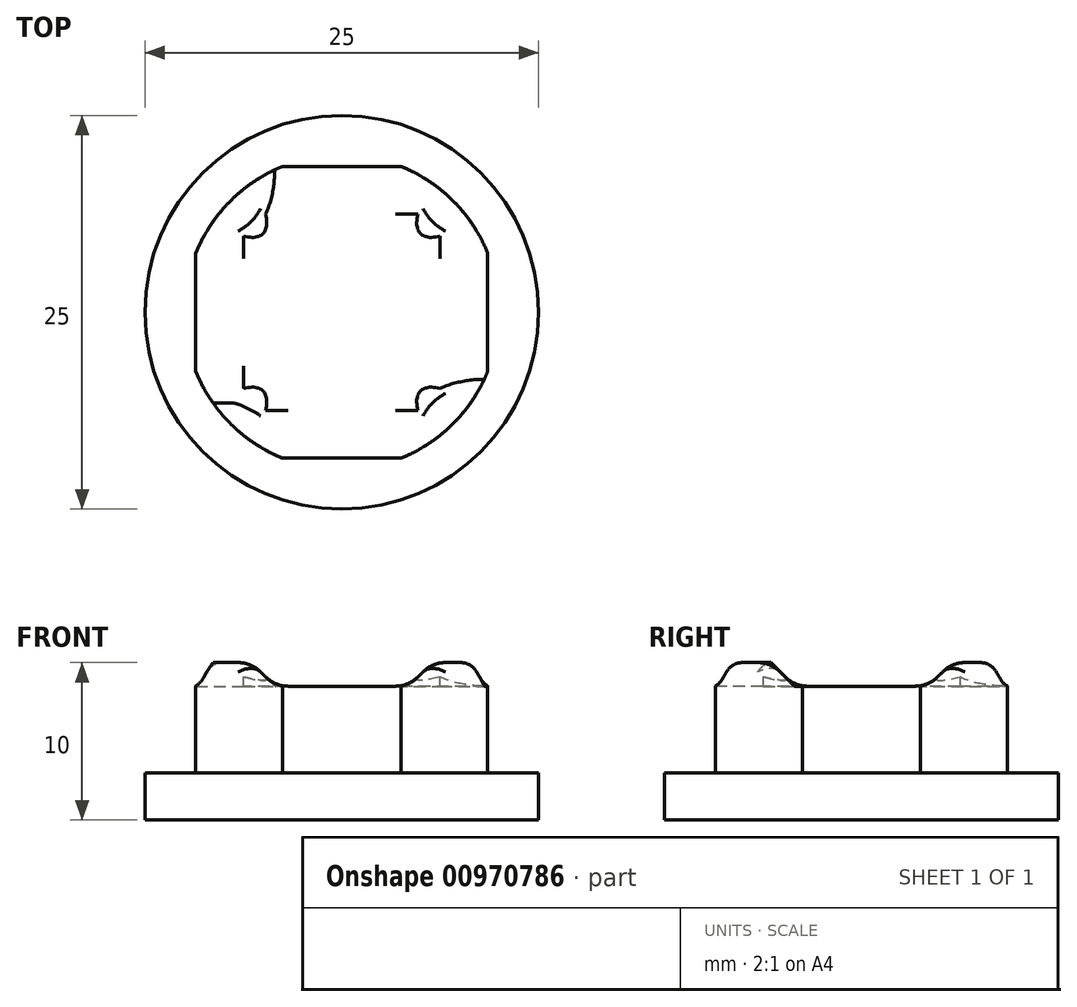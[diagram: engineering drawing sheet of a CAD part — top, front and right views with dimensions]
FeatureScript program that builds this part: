
annotation { "Feature Type Name" : "Feature", "Feature Type Description" : "" }
export const myFeature = defineFeature(function(context is Context, id is Id, definition is map)
    precondition{}
    {
        {
            var Q0;
            Q0=qCreatedBy(makeId("Top.planeOp"),FACE);
            var sketch = newSketch(context, id + "F0", { "sketchPlane" : qUnion([Q0])});
            skCircle(sketch, "E0", {"center": v(0, 0) * mm, "radius": 12.5 * mm});
            skSolve(sketch);
        }
        {
            var Q0;
            Q0 = qSketchRegion(id + "F0", true);
            extrude(context, id + "F1", {"entities" : qUnion([Q0]), "depth" : 3 * mm, "offsetDistance" : 25 * mm});
        }
        {
            var Q0;
            Q0=qCreatedBy(makeId("Top.planeOp"),FACE);
            var sketch = newSketch(context, id + "F2", { "sketchPlane" : qUnion([Q0])});
            skLineSegment(sketch, "E1.bottom", {"start": v(9.27, -3.75) * mm, "end": v(3.75, -3.75) * mm});
            skLineSegment(sketch, "E1.top", {"start": v(9.27, 3.75) * mm, "end": v(3.75, 3.75) * mm});
            skLineSegment(sketch, "E1.left", {"start": v(9.27, -3.75) * mm, "end": v(9.27, 3.75) * mm});
            skLineSegment(sketch, "E1.right", {"start": v(-9.27, -3.75) * mm, "end": v(-9.27, 3.75) * mm});
            skPoint(sketch, "E1.middle", {"position": v(0, 0) * mm});
            skLineSegment(sketch, "E2.bottom", {"start": v(3.75, 9.27) * mm, "end": v(-3.75, 9.27) * mm});
            skLineSegment(sketch, "E2.top", {"start": v(3.75, -9.27) * mm, "end": v(-3.75, -9.27) * mm});
            skLineSegment(sketch, "E2.left", {"start": v(3.75, 9.27) * mm, "end": v(3.75, 3.75) * mm});
            skLineSegment(sketch, "E2.right", {"start": v(-3.75, 9.27) * mm, "end": v(-3.75, 3.75) * mm});
            skLineSegment(sketch, "E3.trimOffspring", {"start": v(-3.75, -3.75) * mm, "end": v(-9.27, -3.75) * mm});
            skLineSegment(sketch, "E4.trimOffspring", {"start": v(-3.75, -3.75) * mm, "end": v(-3.75, -9.27) * mm});
            skLineSegment(sketch, "E5.trimOffspring", {"start": v(-3.75, 3.75) * mm, "end": v(-9.27, 3.75) * mm});
            skLineSegment(sketch, "E6.trimOffspring", {"start": v(3.75, -3.75) * mm, "end": v(3.75, -9.27) * mm});
            skSolve(sketch);
        }
        {
            var Q0;
            Q0 = qSketchRegion(id + "F2", true);
            extrude(context, id + "F3", {"entities" : qUnion([Q0]), "operationType" : NewBodyOperationType.ADD, "depth" : 8.5 * mm, "offsetDistance" : 25 * mm});
        }
        {
            var Q0;
            Q0=qCreatedBy(makeId("Top.planeOp"),FACE);
            var sketch = newSketch(context, id + "F4", { "sketchPlane" : qUnion([Q0])});
            skArc(sketch, "E7", {"start": v(-3.75, 9.27) * mm, "mid": v(-7.07, 7.07) * mm, "end": v(-9.27, 3.75) * mm});
            skLineSegment(sketch, "E8.left", {"start": v(3.75, -9.27) * mm, "end": v(3.75, -3.75) * mm});
            skLineSegment(sketch, "E8.right", {"start": v(-3.75, -9.27) * mm, "end": v(-3.75, -3.75) * mm});
            skLineSegment(sketch, "E9.bottom", {"start": v(9.27, -3.75) * mm, "end": v(3.75, -3.75) * mm});
            skLineSegment(sketch, "E9.top", {"start": v(9.27, 3.75) * mm, "end": v(3.75, 3.75) * mm});
            skLineSegment(sketch, "E10.trimOffspring", {"start": v(-3.75, 3.75) * mm, "end": v(-3.75, 9.27) * mm});
            skLineSegment(sketch, "E11.trimOffspring", {"start": v(-3.75, 3.75) * mm, "end": v(-9.27, 3.75) * mm});
            skLineSegment(sketch, "E12.trimOffspring", {"start": v(3.75, 3.75) * mm, "end": v(3.75, 9.27) * mm});
            skLineSegment(sketch, "E13.trimOffspring", {"start": v(-3.75, -3.75) * mm, "end": v(-9.27, -3.75) * mm});
            skArc(sketch, "E14.trimOffspring", {"start": v(-9.27, -3.75) * mm, "mid": v(-7.07, -7.07) * mm, "end": v(-3.75, -9.27) * mm});
            skArc(sketch, "E15.trimOffspring", {"start": v(3.75, -9.27) * mm, "mid": v(7.07, -7.07) * mm, "end": v(9.27, -3.75) * mm});
            skArc(sketch, "E16.trimOffspring", {"start": v(9.27, 3.75) * mm, "mid": v(7.07, 7.07) * mm, "end": v(3.75, 9.27) * mm});
            skSolve(sketch);
        }
        {
            var Q0;
            Q0 = qSketchRegion(id + "F4", true);
            extrude(context, id + "F5", {"entities" : qUnion([Q0]), "operationType" : NewBodyOperationType.ADD, "depth" : 10 * mm, "offsetDistance" : 25 * mm});
        }
        {
            var Q0;
            Q0=makeQuery(id+"F5.opExtrude","CAP_EDGE",EDGE,{"disambiguationData":[OSD([sQuery(id+"F4.wireOp",EDGE,"E12.trimOffspring")])],"isStart":false});
            chamfer(context, id + "F6", {"entities" : qUnion([Q0]), "width" : 2 * mm, "tangentPropagation" : true});
        }
        {
            var Q0;
            Q0=makeQuery(id+"F5.opExtrude","CAP_EDGE",EDGE,{"disambiguationData":[OSD([sQuery(id+"F4.wireOp",EDGE,"E9.top")])],"isStart":false});
            chamfer(context, id + "F7", {"entities" : qUnion([Q0]), "width" : 2 * mm, "tangentPropagation" : true});
        }
        {
            var Q0;
            Q0=makeQuery(id+"F5.opExtrude","CAP_EDGE",EDGE,{"disambiguationData":[OSD([sQuery(id+"F4.wireOp",EDGE,"E11.trimOffspring")])],"isStart":false});
            var Q1;
            Q1=makeQuery(id+"F5.opExtrude","CAP_EDGE",EDGE,{"disambiguationData":[OSD([sQuery(id+"F4.wireOp",EDGE,"E10.trimOffspring")])],"isStart":false});
            chamfer(context, id + "F8", {"entities" : qUnion([Q0, Q1]), "width" : 2 * mm, "tangentPropagation" : true});
        }
        {
            var Q0;
            Q0=makeQuery(id+"F5.opExtrude","CAP_EDGE",EDGE,{"disambiguationData":[OSD([sQuery(id+"F4.wireOp",EDGE,"E13.trimOffspring")])],"isStart":false});
            var Q1;
            Q1=makeQuery(id+"F5.opExtrude","CAP_EDGE",EDGE,{"disambiguationData":[OSD([sQuery(id+"F4.wireOp",EDGE,"E8.right")])],"isStart":false});
            var Q2;
            Q2=makeQuery(id+"F5.opExtrude","CAP_EDGE",EDGE,{"disambiguationData":[OSD([sQuery(id+"F4.wireOp",EDGE,"E8.left")])],"isStart":false});
            var Q3;
            Q3=makeQuery(id+"F5.opExtrude","CAP_EDGE",EDGE,{"disambiguationData":[OSD([sQuery(id+"F4.wireOp",EDGE,"E9.bottom")])],"isStart":false});
            chamfer(context, id + "F9", {"entities" : qUnion([Q0, Q1, Q2, Q3]), "width" : 2 * mm, "tangentPropagation" : true});
        }
        {
            var Q0;
            Q0=makeQuery(id+"F8.opChamfer","BLEND_EDGE",EDGE,{"blendedFrom":[makeQuery(id+"F5.opExtrude","CAP_EDGE",EDGE,{"disambiguationData":[OSD([sQuery(id+"F4.wireOp",EDGE,"E10.trimOffspring")])],"isStart":false}),makeQuery(id+"F5.opExtrude","CAP_EDGE",EDGE,{"disambiguationData":[OSD([sQuery(id+"F4.wireOp",EDGE,"E11.trimOffspring")])],"isStart":false})],"blendedInto":[]});
            var Q1;
            Q1=makeQuery(id+"F8.opChamfer","BLEND_EDGE",EDGE,{"blendedFrom":[makeQuery(id+"F5.opExtrude","CAP_EDGE",EDGE,{"disambiguationData":[OSD([sQuery(id+"F4.wireOp",EDGE,"E11.trimOffspring")])],"isStart":false}),makeQuery(id+"F3.opExtrude","CAP_FACE",FACE,{"disambiguationData":[OSD([sQuery(id+"F2.wireOp",EDGE,"E1.bottom"),sQuery(id+"F2.wireOp",EDGE,"E1.top"),sQuery(id+"F2.wireOp",EDGE,"E1.left"),sQuery(id+"F2.wireOp",EDGE,"E1.right"),sQuery(id+"F2.wireOp",EDGE,"E2.bottom"),sQuery(id+"F2.wireOp",EDGE,"E2.top"),sQuery(id+"F2.wireOp",EDGE,"E2.left"),sQuery(id+"F2.wireOp",EDGE,"E2.right"),sQuery(id+"F2.wireOp",EDGE,"E3.trimOffspring"),sQuery(id+"F2.wireOp",EDGE,"E4.trimOffspring"),sQuery(id+"F2.wireOp",EDGE,"E5.trimOffspring"),sQuery(id+"F2.wireOp",EDGE,"E6.trimOffspring")])],"isStart":false})],"blendedInto":[makeQuery(id+"F3.opExtrude","CAP_FACE",FACE,{"disambiguationData":[OSD([sQuery(id+"F2.wireOp",EDGE,"E1.bottom"),sQuery(id+"F2.wireOp",EDGE,"E1.top"),sQuery(id+"F2.wireOp",EDGE,"E1.left"),sQuery(id+"F2.wireOp",EDGE,"E1.right"),sQuery(id+"F2.wireOp",EDGE,"E2.bottom"),sQuery(id+"F2.wireOp",EDGE,"E2.top"),sQuery(id+"F2.wireOp",EDGE,"E2.left"),sQuery(id+"F2.wireOp",EDGE,"E2.right"),sQuery(id+"F2.wireOp",EDGE,"E3.trimOffspring"),sQuery(id+"F2.wireOp",EDGE,"E4.trimOffspring"),sQuery(id+"F2.wireOp",EDGE,"E5.trimOffspring"),sQuery(id+"F2.wireOp",EDGE,"E6.trimOffspring")])],"isStart":false})]});
            var Q2;
            {var subQ0=sQuery(id+"F4.wireOp",EDGE,"E11.trimOffspring");Q2=makeQuery(id+"F8.opChamfer","BLEND_EDGE",EDGE,{"blendedFrom":[makeQuery(id+"F5.opExtrude","CAP_EDGE",EDGE,{"disambiguationData":[OSD([subQ0])],"isStart":false}),makeQuery(id+"F5.opExtrude","CAP_FACE",FACE,{"disambiguationData":[OSD([sQuery(id+"F4.wireOp",EDGE,"E7"),sQuery(id+"F4.wireOp",EDGE,"E10.trimOffspring"),subQ0])],"isStart":false})],"blendedInto":[makeQuery(id+"F5.opExtrude","CAP_FACE",FACE,{"disambiguationData":[OSD([sQuery(id+"F4.wireOp",EDGE,"E7"),sQuery(id+"F4.wireOp",EDGE,"E10.trimOffspring"),subQ0])],"isStart":false})]});}
            var Q3;
            {var subQ0=sQuery(id+"F4.wireOp",EDGE,"E10.trimOffspring");Q3=makeQuery(id+"F8.opChamfer","BLEND_EDGE",EDGE,{"blendedFrom":[makeQuery(id+"F5.opExtrude","CAP_EDGE",EDGE,{"disambiguationData":[OSD([subQ0])],"isStart":false}),makeQuery(id+"F5.opExtrude","CAP_FACE",FACE,{"disambiguationData":[OSD([sQuery(id+"F4.wireOp",EDGE,"E7"),subQ0,sQuery(id+"F4.wireOp",EDGE,"E11.trimOffspring")])],"isStart":false})],"blendedInto":[makeQuery(id+"F5.opExtrude","CAP_FACE",FACE,{"disambiguationData":[OSD([sQuery(id+"F4.wireOp",EDGE,"E7"),subQ0,sQuery(id+"F4.wireOp",EDGE,"E11.trimOffspring")])],"isStart":false})]});}
            var Q4;
            Q4=makeQuery(id+"F9.opChamfer","BLEND_EDGE",EDGE,{"blendedFrom":[makeQuery(id+"F5.opExtrude","CAP_EDGE",EDGE,{"disambiguationData":[OSD([sQuery(id+"F4.wireOp",EDGE,"E13.trimOffspring")])],"isStart":false}),makeQuery(id+"F3.opExtrude","CAP_FACE",FACE,{"disambiguationData":[OSD([sQuery(id+"F2.wireOp",EDGE,"E1.bottom"),sQuery(id+"F2.wireOp",EDGE,"E1.top"),sQuery(id+"F2.wireOp",EDGE,"E1.left"),sQuery(id+"F2.wireOp",EDGE,"E1.right"),sQuery(id+"F2.wireOp",EDGE,"E2.bottom"),sQuery(id+"F2.wireOp",EDGE,"E2.top"),sQuery(id+"F2.wireOp",EDGE,"E2.left"),sQuery(id+"F2.wireOp",EDGE,"E2.right"),sQuery(id+"F2.wireOp",EDGE,"E3.trimOffspring"),sQuery(id+"F2.wireOp",EDGE,"E4.trimOffspring"),sQuery(id+"F2.wireOp",EDGE,"E5.trimOffspring"),sQuery(id+"F2.wireOp",EDGE,"E6.trimOffspring")])],"isStart":false})],"blendedInto":[makeQuery(id+"F3.opExtrude","CAP_FACE",FACE,{"disambiguationData":[OSD([sQuery(id+"F2.wireOp",EDGE,"E1.bottom"),sQuery(id+"F2.wireOp",EDGE,"E1.top"),sQuery(id+"F2.wireOp",EDGE,"E1.left"),sQuery(id+"F2.wireOp",EDGE,"E1.right"),sQuery(id+"F2.wireOp",EDGE,"E2.bottom"),sQuery(id+"F2.wireOp",EDGE,"E2.top"),sQuery(id+"F2.wireOp",EDGE,"E2.left"),sQuery(id+"F2.wireOp",EDGE,"E2.right"),sQuery(id+"F2.wireOp",EDGE,"E3.trimOffspring"),sQuery(id+"F2.wireOp",EDGE,"E4.trimOffspring"),sQuery(id+"F2.wireOp",EDGE,"E5.trimOffspring"),sQuery(id+"F2.wireOp",EDGE,"E6.trimOffspring")])],"isStart":false})]});
            var Q5;
            Q5=makeQuery(id+"F9.opChamfer","BLEND_EDGE",EDGE,{"blendedFrom":[makeQuery(id+"F5.opExtrude","CAP_EDGE",EDGE,{"disambiguationData":[OSD([sQuery(id+"F4.wireOp",EDGE,"E8.right")])],"isStart":false}),makeQuery(id+"F3.opExtrude","CAP_FACE",FACE,{"disambiguationData":[OSD([sQuery(id+"F2.wireOp",EDGE,"E1.bottom"),sQuery(id+"F2.wireOp",EDGE,"E1.top"),sQuery(id+"F2.wireOp",EDGE,"E1.left"),sQuery(id+"F2.wireOp",EDGE,"E1.right"),sQuery(id+"F2.wireOp",EDGE,"E2.bottom"),sQuery(id+"F2.wireOp",EDGE,"E2.top"),sQuery(id+"F2.wireOp",EDGE,"E2.left"),sQuery(id+"F2.wireOp",EDGE,"E2.right"),sQuery(id+"F2.wireOp",EDGE,"E3.trimOffspring"),sQuery(id+"F2.wireOp",EDGE,"E4.trimOffspring"),sQuery(id+"F2.wireOp",EDGE,"E5.trimOffspring"),sQuery(id+"F2.wireOp",EDGE,"E6.trimOffspring")])],"isStart":false})],"blendedInto":[makeQuery(id+"F3.opExtrude","CAP_FACE",FACE,{"disambiguationData":[OSD([sQuery(id+"F2.wireOp",EDGE,"E1.bottom"),sQuery(id+"F2.wireOp",EDGE,"E1.top"),sQuery(id+"F2.wireOp",EDGE,"E1.left"),sQuery(id+"F2.wireOp",EDGE,"E1.right"),sQuery(id+"F2.wireOp",EDGE,"E2.bottom"),sQuery(id+"F2.wireOp",EDGE,"E2.top"),sQuery(id+"F2.wireOp",EDGE,"E2.left"),sQuery(id+"F2.wireOp",EDGE,"E2.right"),sQuery(id+"F2.wireOp",EDGE,"E3.trimOffspring"),sQuery(id+"F2.wireOp",EDGE,"E4.trimOffspring"),sQuery(id+"F2.wireOp",EDGE,"E5.trimOffspring"),sQuery(id+"F2.wireOp",EDGE,"E6.trimOffspring")])],"isStart":false})]});
            var Q6;
            Q6=makeQuery(id+"F9.opChamfer","BLEND_EDGE",EDGE,{"blendedFrom":[makeQuery(id+"F5.opExtrude","CAP_EDGE",EDGE,{"disambiguationData":[OSD([sQuery(id+"F4.wireOp",EDGE,"E8.right")])],"isStart":false}),makeQuery(id+"F5.opExtrude","CAP_EDGE",EDGE,{"disambiguationData":[OSD([sQuery(id+"F4.wireOp",EDGE,"E13.trimOffspring")])],"isStart":false})],"blendedInto":[]});
            var Q7;
            {var subQ0=sQuery(id+"F4.wireOp",EDGE,"E8.right");Q7=makeQuery(id+"F9.opChamfer","BLEND_EDGE",EDGE,{"blendedFrom":[makeQuery(id+"F5.opExtrude","CAP_EDGE",EDGE,{"disambiguationData":[OSD([subQ0])],"isStart":false}),makeQuery(id+"F5.opExtrude","CAP_FACE",FACE,{"disambiguationData":[OSD([subQ0,sQuery(id+"F4.wireOp",EDGE,"E13.trimOffspring"),sQuery(id+"F4.wireOp",EDGE,"E14.trimOffspring")])],"isStart":false})],"blendedInto":[makeQuery(id+"F5.opExtrude","CAP_FACE",FACE,{"disambiguationData":[OSD([subQ0,sQuery(id+"F4.wireOp",EDGE,"E13.trimOffspring"),sQuery(id+"F4.wireOp",EDGE,"E14.trimOffspring")])],"isStart":false})]});}
            var Q8;
            {var subQ0=sQuery(id+"F4.wireOp",EDGE,"E9.bottom");Q8=makeQuery(id+"F9.opChamfer","BLEND_EDGE",EDGE,{"blendedFrom":[makeQuery(id+"F5.opExtrude","CAP_EDGE",EDGE,{"disambiguationData":[OSD([subQ0])],"isStart":false}),makeQuery(id+"F5.opExtrude","CAP_FACE",FACE,{"disambiguationData":[OSD([sQuery(id+"F4.wireOp",EDGE,"E8.left"),subQ0,sQuery(id+"F4.wireOp",EDGE,"E15.trimOffspring")])],"isStart":false})],"blendedInto":[makeQuery(id+"F5.opExtrude","CAP_FACE",FACE,{"disambiguationData":[OSD([sQuery(id+"F4.wireOp",EDGE,"E8.left"),subQ0,sQuery(id+"F4.wireOp",EDGE,"E15.trimOffspring")])],"isStart":false})]});}
            var Q9;
            {var subQ0=sQuery(id+"F4.wireOp",EDGE,"E8.left");Q9=makeQuery(id+"F9.opChamfer","BLEND_EDGE",EDGE,{"blendedFrom":[makeQuery(id+"F5.opExtrude","CAP_EDGE",EDGE,{"disambiguationData":[OSD([subQ0])],"isStart":false}),makeQuery(id+"F5.opExtrude","CAP_FACE",FACE,{"disambiguationData":[OSD([subQ0,sQuery(id+"F4.wireOp",EDGE,"E9.bottom"),sQuery(id+"F4.wireOp",EDGE,"E15.trimOffspring")])],"isStart":false})],"blendedInto":[makeQuery(id+"F5.opExtrude","CAP_FACE",FACE,{"disambiguationData":[OSD([subQ0,sQuery(id+"F4.wireOp",EDGE,"E9.bottom"),sQuery(id+"F4.wireOp",EDGE,"E15.trimOffspring")])],"isStart":false})]});}
            var Q10;
            Q10=makeQuery(id+"F9.opChamfer","BLEND_EDGE",EDGE,{"blendedFrom":[makeQuery(id+"F5.opExtrude","CAP_EDGE",EDGE,{"disambiguationData":[OSD([sQuery(id+"F4.wireOp",EDGE,"E8.left")])],"isStart":false}),makeQuery(id+"F5.opExtrude","CAP_EDGE",EDGE,{"disambiguationData":[OSD([sQuery(id+"F4.wireOp",EDGE,"E9.bottom")])],"isStart":false})],"blendedInto":[]});
            var Q11;
            Q11=makeQuery(id+"F9.opChamfer","BLEND_EDGE",EDGE,{"blendedFrom":[makeQuery(id+"F5.opExtrude","CAP_EDGE",EDGE,{"disambiguationData":[OSD([sQuery(id+"F4.wireOp",EDGE,"E8.left")])],"isStart":false}),makeQuery(id+"F3.opExtrude","CAP_FACE",FACE,{"disambiguationData":[OSD([sQuery(id+"F2.wireOp",EDGE,"E1.bottom"),sQuery(id+"F2.wireOp",EDGE,"E1.top"),sQuery(id+"F2.wireOp",EDGE,"E1.left"),sQuery(id+"F2.wireOp",EDGE,"E1.right"),sQuery(id+"F2.wireOp",EDGE,"E2.bottom"),sQuery(id+"F2.wireOp",EDGE,"E2.top"),sQuery(id+"F2.wireOp",EDGE,"E2.left"),sQuery(id+"F2.wireOp",EDGE,"E2.right"),sQuery(id+"F2.wireOp",EDGE,"E3.trimOffspring"),sQuery(id+"F2.wireOp",EDGE,"E4.trimOffspring"),sQuery(id+"F2.wireOp",EDGE,"E5.trimOffspring"),sQuery(id+"F2.wireOp",EDGE,"E6.trimOffspring")])],"isStart":false})],"blendedInto":[makeQuery(id+"F3.opExtrude","CAP_FACE",FACE,{"disambiguationData":[OSD([sQuery(id+"F2.wireOp",EDGE,"E1.bottom"),sQuery(id+"F2.wireOp",EDGE,"E1.top"),sQuery(id+"F2.wireOp",EDGE,"E1.left"),sQuery(id+"F2.wireOp",EDGE,"E1.right"),sQuery(id+"F2.wireOp",EDGE,"E2.bottom"),sQuery(id+"F2.wireOp",EDGE,"E2.top"),sQuery(id+"F2.wireOp",EDGE,"E2.left"),sQuery(id+"F2.wireOp",EDGE,"E2.right"),sQuery(id+"F2.wireOp",EDGE,"E3.trimOffspring"),sQuery(id+"F2.wireOp",EDGE,"E4.trimOffspring"),sQuery(id+"F2.wireOp",EDGE,"E5.trimOffspring"),sQuery(id+"F2.wireOp",EDGE,"E6.trimOffspring")])],"isStart":false})]});
            var Q12;
            Q12=makeQuery(id+"F7.opChamfer","BLEND_EDGE",EDGE,{"blendedFrom":[makeQuery(id+"F5.opExtrude","CAP_EDGE",EDGE,{"disambiguationData":[OSD([sQuery(id+"F4.wireOp",EDGE,"E9.top")])],"isStart":false}),makeQuery(id+"F3.opExtrude","CAP_FACE",FACE,{"disambiguationData":[OSD([sQuery(id+"F2.wireOp",EDGE,"E1.bottom"),sQuery(id+"F2.wireOp",EDGE,"E1.top"),sQuery(id+"F2.wireOp",EDGE,"E1.left"),sQuery(id+"F2.wireOp",EDGE,"E1.right"),sQuery(id+"F2.wireOp",EDGE,"E2.bottom"),sQuery(id+"F2.wireOp",EDGE,"E2.top"),sQuery(id+"F2.wireOp",EDGE,"E2.left"),sQuery(id+"F2.wireOp",EDGE,"E2.right"),sQuery(id+"F2.wireOp",EDGE,"E3.trimOffspring"),sQuery(id+"F2.wireOp",EDGE,"E4.trimOffspring"),sQuery(id+"F2.wireOp",EDGE,"E5.trimOffspring"),sQuery(id+"F2.wireOp",EDGE,"E6.trimOffspring")])],"isStart":false})],"blendedInto":[makeQuery(id+"F3.opExtrude","CAP_FACE",FACE,{"disambiguationData":[OSD([sQuery(id+"F2.wireOp",EDGE,"E1.bottom"),sQuery(id+"F2.wireOp",EDGE,"E1.top"),sQuery(id+"F2.wireOp",EDGE,"E1.left"),sQuery(id+"F2.wireOp",EDGE,"E1.right"),sQuery(id+"F2.wireOp",EDGE,"E2.bottom"),sQuery(id+"F2.wireOp",EDGE,"E2.top"),sQuery(id+"F2.wireOp",EDGE,"E2.left"),sQuery(id+"F2.wireOp",EDGE,"E2.right"),sQuery(id+"F2.wireOp",EDGE,"E3.trimOffspring"),sQuery(id+"F2.wireOp",EDGE,"E4.trimOffspring"),sQuery(id+"F2.wireOp",EDGE,"E5.trimOffspring"),sQuery(id+"F2.wireOp",EDGE,"E6.trimOffspring")])],"isStart":false})]});
            var Q13;
            Q13=makeQuery(id+"F6.opChamfer","BLEND_EDGE",EDGE,{"blendedFrom":[makeQuery(id+"F5.opExtrude","CAP_EDGE",EDGE,{"disambiguationData":[OSD([sQuery(id+"F4.wireOp",EDGE,"E12.trimOffspring")])],"isStart":false}),makeQuery(id+"F3.opExtrude","CAP_FACE",FACE,{"disambiguationData":[OSD([sQuery(id+"F2.wireOp",EDGE,"E1.bottom"),sQuery(id+"F2.wireOp",EDGE,"E1.top"),sQuery(id+"F2.wireOp",EDGE,"E1.left"),sQuery(id+"F2.wireOp",EDGE,"E1.right"),sQuery(id+"F2.wireOp",EDGE,"E2.bottom"),sQuery(id+"F2.wireOp",EDGE,"E2.top"),sQuery(id+"F2.wireOp",EDGE,"E2.left"),sQuery(id+"F2.wireOp",EDGE,"E2.right"),sQuery(id+"F2.wireOp",EDGE,"E3.trimOffspring"),sQuery(id+"F2.wireOp",EDGE,"E4.trimOffspring"),sQuery(id+"F2.wireOp",EDGE,"E5.trimOffspring"),sQuery(id+"F2.wireOp",EDGE,"E6.trimOffspring")])],"isStart":false})],"blendedInto":[makeQuery(id+"F3.opExtrude","CAP_FACE",FACE,{"disambiguationData":[OSD([sQuery(id+"F2.wireOp",EDGE,"E1.bottom"),sQuery(id+"F2.wireOp",EDGE,"E1.top"),sQuery(id+"F2.wireOp",EDGE,"E1.left"),sQuery(id+"F2.wireOp",EDGE,"E1.right"),sQuery(id+"F2.wireOp",EDGE,"E2.bottom"),sQuery(id+"F2.wireOp",EDGE,"E2.top"),sQuery(id+"F2.wireOp",EDGE,"E2.left"),sQuery(id+"F2.wireOp",EDGE,"E2.right"),sQuery(id+"F2.wireOp",EDGE,"E3.trimOffspring"),sQuery(id+"F2.wireOp",EDGE,"E4.trimOffspring"),sQuery(id+"F2.wireOp",EDGE,"E5.trimOffspring"),sQuery(id+"F2.wireOp",EDGE,"E6.trimOffspring")])],"isStart":false})]});
            var Q14;
            Q14=makeQuery(id+"F7.opChamfer","BLEND_EDGE",EDGE,{"blendedFrom":[makeQuery(id+"F5.opExtrude","CAP_EDGE",EDGE,{"disambiguationData":[OSD([sQuery(id+"F4.wireOp",EDGE,"E9.top")])],"isStart":false}),makeQuery(id+"F6.opChamfer","BLEND_FACE",FACE,{"disambiguationData":[OSD([sQuery(id+"F4.wireOp",EDGE,"E12.trimOffspring")])]})],"blendedInto":[makeQuery(id+"F6.opChamfer","BLEND_FACE",FACE,{"disambiguationData":[OSD([sQuery(id+"F4.wireOp",EDGE,"E12.trimOffspring")])]})]});
            var Q15;
            {var subQ0=sQuery(id+"F4.wireOp",EDGE,"E9.top");Q15=makeQuery(id+"F7.opChamfer","BLEND_EDGE",EDGE,{"blendedFrom":[makeQuery(id+"F5.opExtrude","CAP_EDGE",EDGE,{"disambiguationData":[OSD([subQ0])],"isStart":false}),makeQuery(id+"F5.opExtrude","CAP_FACE",FACE,{"disambiguationData":[OSD([subQ0,sQuery(id+"F4.wireOp",EDGE,"E12.trimOffspring"),sQuery(id+"F4.wireOp",EDGE,"E16.trimOffspring")])],"isStart":false})],"blendedInto":[makeQuery(id+"F5.opExtrude","CAP_FACE",FACE,{"disambiguationData":[OSD([subQ0,sQuery(id+"F4.wireOp",EDGE,"E12.trimOffspring"),sQuery(id+"F4.wireOp",EDGE,"E16.trimOffspring")])],"isStart":false})]});}
            var Q16;
            {var subQ0=sQuery(id+"F4.wireOp",EDGE,"E12.trimOffspring");Q16=makeQuery(id+"F6.opChamfer","BLEND_EDGE",EDGE,{"blendedFrom":[makeQuery(id+"F5.opExtrude","CAP_EDGE",EDGE,{"disambiguationData":[OSD([subQ0])],"isStart":false}),makeQuery(id+"F5.opExtrude","CAP_FACE",FACE,{"disambiguationData":[OSD([sQuery(id+"F4.wireOp",EDGE,"E9.top"),subQ0,sQuery(id+"F4.wireOp",EDGE,"E16.trimOffspring")])],"isStart":false})],"blendedInto":[makeQuery(id+"F5.opExtrude","CAP_FACE",FACE,{"disambiguationData":[OSD([sQuery(id+"F4.wireOp",EDGE,"E9.top"),subQ0,sQuery(id+"F4.wireOp",EDGE,"E16.trimOffspring")])],"isStart":false})]});}
            fillet(context, id + "F10", {"entities" : qUnion([Q0, Q1, Q2, Q3, Q4, Q5, Q6, Q7, Q8, Q9, Q10, Q11, Q12, Q13, Q14, Q15, Q16]), "radius" : 2 * mm, "tangentPropagation" : true, "allowEdgeOverflow" : false});
        }
    });
